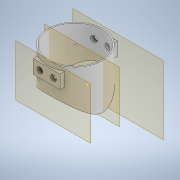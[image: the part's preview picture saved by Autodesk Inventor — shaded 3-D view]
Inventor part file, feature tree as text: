
AUTODESK INVENTOR PART (.ipt)
format: ipt  version: 2020 (Build 240168000, 168)  size: 176,640 bytes
history: native  units: mm
features: sketch x6, extrude x4, plane x2, mirror x1, projected_geometry x1
ambient origin geometry x8: Origin, YZ Plane, XZ Plane, XY Plane, X Axis, Y Axis, Z Axis, Center Point
bodies: Solid1 (feature_tree)
feature tree (14):
  extrude  "Extrusion1"  Depth=24.0mm TaperAngle=0.0deg
  plane  "Work Plane1"
  sketch  "Sketch3"  dims[d7=-29.0mm d8=72.25mm d9=0.0mm]
  extrude  "Extrusion3"  Depth=72.25mm TaperAngle=0.0deg
  sketch  "Sketch5"  dims[d12=72.25mm d13=0.0mm d14=7.0mm]
  plane  "Work Plane2"
  mirror  "Mirror1"
  extrude  "Extrusion4"  Depth=3.0mm
  extrude  "Extrusion5"  Depth=7.0mm
  sketch  "Sketch1"  dims[d0=0.6mm d1=24.0mm d2=0.0mm]
  sketch  "Sketch4"  dims[d10=3.0mm d11=3.0mm]
  sketch  "Sketch6"  dims[d15=32.931mm]
  projected_geometry  "Projected Loop2"
  sketch  "Sketch7"  dims[d16=60.25mm d17=0.0mm]
